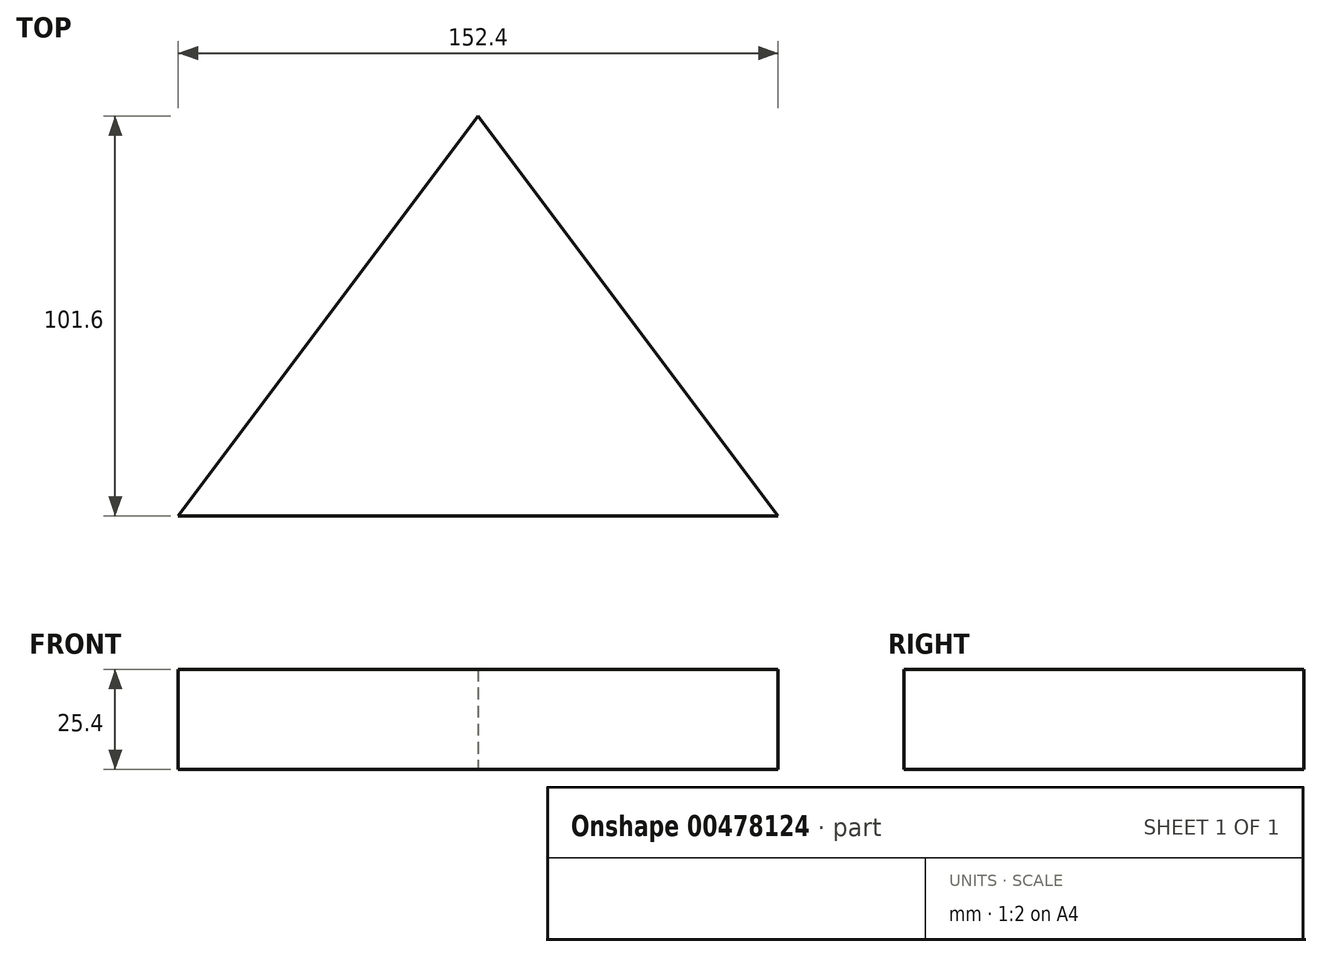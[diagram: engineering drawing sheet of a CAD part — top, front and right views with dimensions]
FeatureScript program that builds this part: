
annotation { "Feature Type Name" : "Feature", "Feature Type Description" : "" }
export const myFeature = defineFeature(function(context is Context, id is Id, definition is map)
    precondition{}
    {
        {
            var Q0;
            Q0=qCreatedBy(makeId("Top.planeOp"),FACE);
            var sketch = newSketch(context, id + "F0", { "sketchPlane" : qUnion([Q0])});
            skLineSegment(sketch, "E0", {"start": v(0, 0) * mm, "end": v(152.4, 0) * mm});
            skLineSegment(sketch, "E1", {"start": v(76.2, 0) * mm, "end": v(76.2, 101.6) * mm});
            skLineSegment(sketch, "E2", {"start": v(76.2, 101.6) * mm, "end": v(0, 0) * mm});
            skLineSegment(sketch, "E3", {"start": v(76.2, 101.6) * mm, "end": v(152.4, 0) * mm});
            skSolve(sketch);
        }
        {
            var Q0;
            {var subQ2=sQuery(id+"F0.wireOp",EDGE,"E1");Q0=makeQuery(id+"F0.imprint","IMPRINT",FACE,{"disambiguationData":[TD([[makeQuery(id+"F0.imprint","IMPRINT",EDGE,{"derivedFrom":subQ2}),-1.0]])]});}
            var Q1;
            {var subQ2=sQuery(id+"F0.wireOp",EDGE,"E1");Q1=makeQuery(id+"F0.imprint","IMPRINT",FACE,{"disambiguationData":[TD([[makeQuery(id+"F0.imprint","IMPRINT",EDGE,{"derivedFrom":subQ2}),1.0]])]});}
            extrude(context, id + "F1", {"entities" : qUnion([Q0, Q1]), "depth" : 25.4 * mm, "offsetDistance" : 25.4 * mm});
        }
    });
